# Revit family: URA Eclairage de Séurité_PLASTINOX
name_source: partatom
category: Luminaires
units: mm (PartAtom-declared; Revit-internal decimal feet)

## family parameters
Cote de connecteur circulaire = Utiliser le diamètre
Couper avec des vides une fois chargée = Non
Hôte = Face
Partagée = Non
Repere pour localisation dans la piece = Non
Source d'éclairage = Non
Type d'élément = Normal

## types (2) — shared parameters
Adressable = Oui
Alimentation de secours = Autonome (batterie individuelle)
Autonomie = 1 H
Batterie de rechange = UR111921
Classe ETIM = EC001957-Luminaire d'éclairage de sécurité
Classe de protection = II
Conditions Générale d'Utilisation = https://export.legrand.com
Consommation en veille = 0 A
Couleur = Blanc
Elévation par défaut = 2300 mm
Fabricant = URA
Fréquence = 50/60 Hz
Hauteur = 100 mm  [stored 0.328084 ft]
IK = 10
IP = 68
Largeur = 100 mm  [stored 0.328084 ft]
Longueur = 340 mm  [stored 1.11549 ft]
Matière = Plastique
Mode de pose = Montage en saillie (mur_plafond)
Objet Connecté = Non
Puissance du système = 1 VA
Système de contrôle = Auto-test automatique
Temperature d'utilisation MIN-MAX = 0°C +35°C
Tension = 230 VAC
Type de commutation = Non permanent
Type de connexion = autre
capacité des bornes = 1,5 mm2
source lumineuse = LED non interchangeable
état des accus = NiMh

## per-type parameters (varying)
| type | Anti panique | Code EAN | Description Produit | Evac | Flux lumineux utile | Fonction | Référence / Modèle | Type de pictogramme |
| Evacuation | Non | 3613400171606 | BAES EVACUATION PLASTINOX 100LM-1H SATI CONNECTE-ADRESSABLE IP68-69-IK10 | Oui | 100 lm | Éclairage d'évacuation | UR117719V | Feuillet/plaque inséré(e) |
| Antipanique | Oui | 3613400171545 | BAES AMBIANCE PLASTINOX 450LM-1H SATI CONNECTE-ADRESSABLE IP68-69-IK10 | Non | 450 lm | Éclairage d'ambiance (anti-panique) | UR117729V |  |

note: [stored X ft] marks values corroborated as IEEE doubles in the binary element streams (Revit-internal decimal feet)
